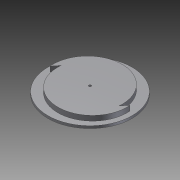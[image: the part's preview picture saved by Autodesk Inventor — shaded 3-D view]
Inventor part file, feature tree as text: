
AUTODESK INVENTOR PART (.ipt)
format: ipt  version: 2011 (Build 150239000, 239)  size: 99,328 bytes
history: native  units: mm
features: extrude x2, sketch x2, other x1
ambient origin geometry x8: Origin, YZ Plane, XZ Plane, XY Plane, X Axis, Y Axis, Z Axis, Center Point
feature tree (5):
  other  "Sólido1"
  extrude  "Extrusión1"  Depth=1.0mm
  extrude  "Extrusión2"  Depth=28.0mm
  sketch  "Boceto1"  dims[d0=34.0mm d1=1.0mm]
  sketch  "Boceto2"  dims[d2=1.0mm d3=0.0mm d15=28.0mm d16=14.0mm d18=14.0mm d19=0.872665mm d20=14.0mm d21=0.872665mm d22=20.0mm d24=360.0deg d26=15.0mm d27=2.0mm d28=0.0mm]
